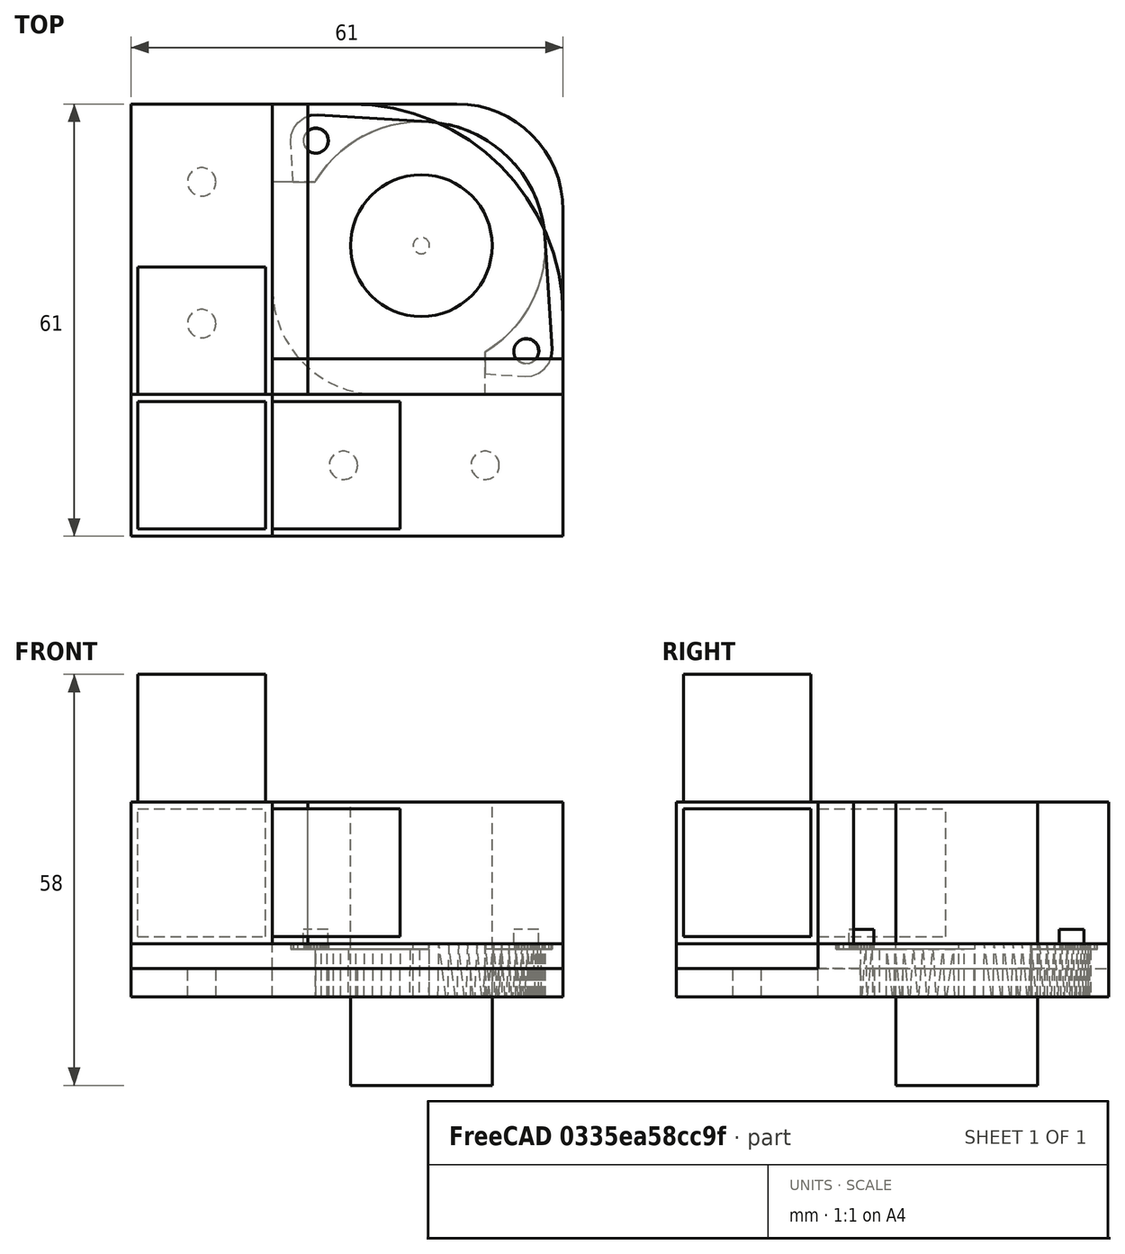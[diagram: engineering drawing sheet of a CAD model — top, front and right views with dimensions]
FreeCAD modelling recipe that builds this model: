
FCSTD DOCUMENT  (FreeCAD 0.19R24276 (Git))
Label: motorCoreXY
License: All rights reserved
LicenseURL: http://en.wikipedia.org/wiki/All_rights_reserved
objects: Part::Box×12, Part::Cut×10, Part::Cylinder×8, Part::Fuse×5, Part::Fillet×3, Mesh::Feature×1, Part::Feature×1
note: 39 computed .brp shape members not serialized (recipe doc carries the construction recipe); baked Part::Feature solids carry a one-line shape summary decoded from their .brp

FEATURE [Part::Box] Box  label="central"
  AttacherType = Attacher::AttachEngine3D
  Height = 20
  Length = 20
  Width = 20
FEATURE [Part::Box] Box001  label="X"
  AttacherType = Attacher::AttachEngine3D
  Height = 18
  Length = 18
  Placement = pos=(20,1,1) rot=(0,0,1;0rad)
  Width = 18
FEATURE [Part::Fuse] Fusion
  Base = -> Box
  Tool = -> Box001
FEATURE [Mesh::Feature] motor_Mitsumi_M35SP_11NK  label="motor_Mitsumi_M35SP-11NK"
  Placement = pos=(25,25,-1) rot=(0,0,1;-0.785398rad)
FEATURE [Part::Box] Box003  label="Z"
  AttacherType = Attacher::AttachEngine3D
  Height = 18
  Length = 18
  Placement = pos=(1,1,20) rot=(0,0,1;0rad)
  Width = 18
FEATURE [Part::Box] Box002  label="Y"
  AttacherType = Attacher::AttachEngine3D
  Height = 18
  Length = 18
  Placement = pos=(1,20,1) rot=(0,0,1;0rad)
  Width = 18
FEATURE [Part::Fuse] Fusion001
  Base = -> Fusion
  Tool = -> Box002
FEATURE [Part::Fuse] Fusion002  label="UnionXYZ"
  Base = -> Fusion001
  Tool = -> Box003
FEATURE [Part::Feature] motor_Mitsumi_M35SP_11NK001_solid  label="motor_Mitsumi_M35SP_11NK001 (Solid)"
  Placement = pos=(16,16,0.2) rot=(0,0,1;0rad)
  shape: bbox 36.88 x 36.88 x 16.9 mm, 3172 faces (baked)
FEATURE [Part::Box] Box005  label="Cube001"
  AttacherType = Attacher::AttachEngine3D
  Height = 7.5
  Length = 61
  Placement = pos=(0,0,-7.5) rot=(0,0,1;0rad)
  Width = 61
FEATURE [Part::Cut] Cut
  Base = -> Box005
  Tool = -> motor_Mitsumi_M35SP_11NK001_solid
FEATURE [Part::Fillet] Fillet
  Base = -> Cut
  Edges = 1 edges r=15: [Edge63]
FEATURE [Part::Cylinder] Cylinder
  Angle = 360
  AttacherType = Attacher::AttachEngine3D
  Height = 50
  Placement = pos=(10,50,-20) rot=(0,0,1;0rad)
  Radius = 2
FEATURE [Part::Cylinder] Cylinder001
  Angle = 360
  AttacherType = Attacher::AttachEngine3D
  Height = 50
  Placement = pos=(10,30,-20) rot=(0,0,1;0rad)
  Radius = 2
FEATURE [Part::Box] Box006  label="Cube"
  AttacherType = Attacher::AttachEngine3D
  Height = 20
  Length = 20
  Placement = pos=(0,0,-3.5) rot=(0,0,1;0rad)
  Width = 70
FEATURE [Part::Box] Box007  label="Cube002"
  AttacherType = Attacher::AttachEngine3D
  Height = 20
  Length = 70
  Placement = pos=(0,0,-3.5) rot=(0,0,1;0rad)
  Width = 20
FEATURE [Part::Cut] Cut001
  Base = -> Fillet
  Tool = -> Box006
FEATURE [Part::Cut] Cut002
  Base = -> Cut001
  Tool = -> Box007
FEATURE [Part::Cut] Cut003
  Base = -> Cut002
  Tool = -> Cylinder001
FEATURE [Part::Cut] Cut004
  Base = -> Cut003
  Tool = -> Cylinder
FEATURE [Part::Cylinder] Cylinder002
  Angle = 360
  AttacherType = Attacher::AttachEngine3D
  Height = 40
  Placement = pos=(30,10,-20) rot=(0,0,1;0rad)
  Radius = 2
FEATURE [Part::Cylinder] Cylinder003
  Angle = 360
  AttacherType = Attacher::AttachEngine3D
  Height = 40
  Placement = pos=(50,10,-20) rot=(0,0,1;0rad)
  Radius = 2
FEATURE [Part::Cut] Cut005
  Base = -> Cut004
  Tool = -> Cylinder002
FEATURE [Part::Cut] Cut006  label="cutConAgujeros"
  Base = -> Cut005
  Tool = -> Cylinder003
FEATURE [Part::Box] Box008  label="Cube003"
  AttacherType = Attacher::AttachEngine3D
  Height = 40
  Length = 30
  Placement = pos=(20,20,-15) rot=(0,0,1;0rad)
  Width = 30
FEATURE [Part::Fillet] Fillet001
  Base = -> Box008
  Edges = 1 edges r=15: [Edge1]
FEATURE [Part::Cut] Cut007
  Base = -> Cut006
  Tool = -> Fillet001
FEATURE [Part::Box] Box009  label="Cube004"
  AttacherType = Attacher::AttachEngine3D
  Height = 10
  Length = 20
  Placement = pos=(20,20,-3.5) rot=(0,0,1;0rad)
  Width = 20
FEATURE [Part::Cut] Cut008
  Base = -> Cut007
  Tool = -> Box009
FEATURE [Part::Cylinder] Cylinder004
  Angle = 360
  AttacherType = Attacher::AttachEngine3D
  Height = 2
  Placement = pos=(55.8,26.1,0) rot=(0,0,1;0rad)
  Radius = 1.75
FEATURE [Part::Cylinder] Cylinder005
  Angle = 360
  AttacherType = Attacher::AttachEngine3D
  Height = 2
  Placement = pos=(26.1,55.8,0) rot=(0,0,1;0rad)
  Radius = 1.75
FEATURE [Part::Fuse] Fusion003
  Base = -> Cut008
  Tool = -> Cylinder004
FEATURE [Part::Fuse] Fusion004  label="MotorCoreXY"
  Base = -> Cylinder005
  Tool = -> Fusion003
FEATURE [Part::Box] Box010  label="Cube005"
  AttacherType = Attacher::AttachEngine3D
  Height = 7.5
  Length = 61
  Placement = pos=(0,0,-7.5) rot=(0,0,1;0rad)
  Width = 61
FEATURE [Part::Box] Box011  label="Cube006"
  AttacherType = Attacher::AttachEngine3D
  Height = 20
  Length = 41
  Placement = pos=(20,20,0) rot=(0,0,1;0rad)
  Width = 5
FEATURE [Part::Cylinder] Cylinder006  label="EjeRodamientos"
  Angle = 360
  AttacherType = Attacher::AttachEngine3D
  Height = 40
  Placement = pos=(41,41,-20) rot=(0,0,1;0rad)
  Radius = 1.15
FEATURE [Part::Fillet] Fillet002
  Base = -> Box010
  Edges = 1 edges r=30: [Edge7]
FEATURE [Part::Cut] Cut009
  Base = -> Fillet002
  Tool = -> Cylinder006
FEATURE [Part::Box] Box012  label="Cube007"
  AttacherType = Attacher::AttachEngine3D
  Height = 20
  Length = 5
  Placement = pos=(20,20,0) rot=(0,0,1;0rad)
  Width = 41
FEATURE [Part::Cylinder] Cylinder007  label="EjeRodamientos001"
  Angle = 360
  AttacherType = Attacher::AttachEngine3D
  Height = 40
  Placement = pos=(41,41,-20) rot=(0,0,1;0rad)
  Radius = 10
